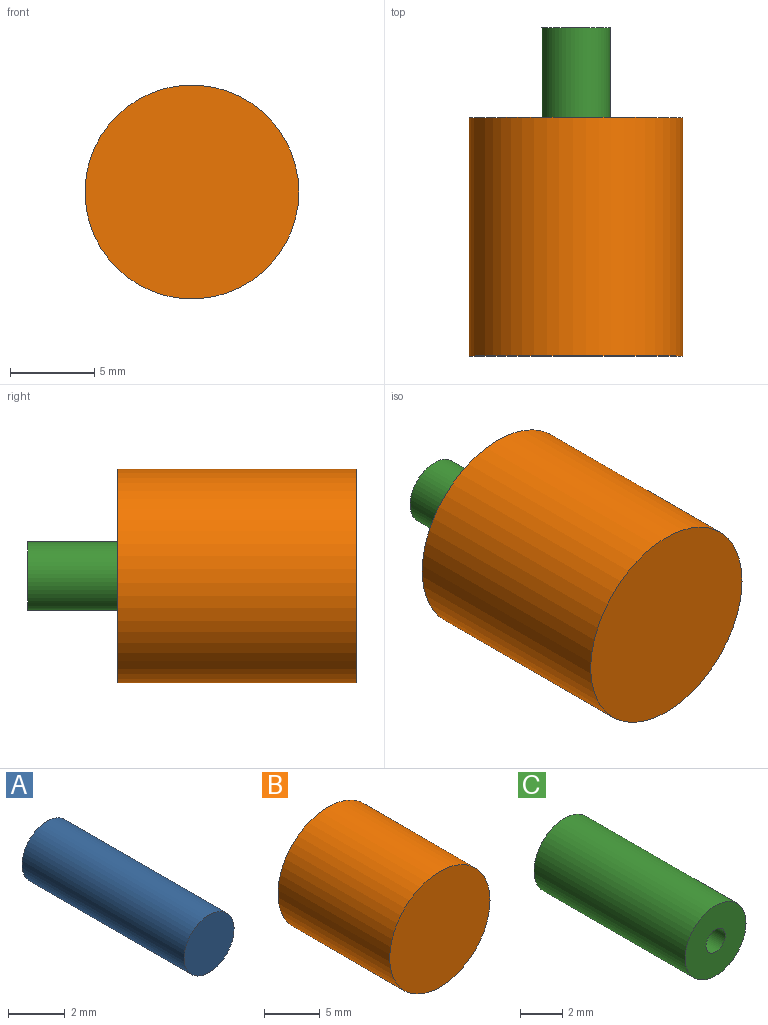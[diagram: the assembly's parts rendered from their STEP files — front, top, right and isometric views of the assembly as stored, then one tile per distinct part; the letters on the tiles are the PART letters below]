
ASSEMBLY  parts=3 mates=1
PART A: 3 faces, bbox 2.5x8.1x2.5 mm
  f0: cylinder r=1.24mm len=8.08mm, axis (0,1,0), area 63.2mm2, adj f1,f2
  f1: plane 2.49x2.49mm, normal (0,-1,0), area 4.9mm2, adj f0
  f2: plane 2.49x2.49mm, normal (0,1,0), area 4.9mm2, adj f0
PART B: 5 faces, bbox 12.7x14.2x12.7 mm
  f0: cylinder r=2.11mm len=4.83mm, axis (0,1,0), area 63.9mm2, adj f2,f3
  f1: cylinder r=6.35mm len=14.16mm, axis (0,1,0), area 565mm2, adj f2,f4
  f2: plane 12.7x12.7mm, normal (0,1,0), area 112.7mm2, adj f0,f1
  f3: plane 4.22x4.22mm, normal (0,1,0), area 14mm2, adj f0
  f4: plane 12.7x12.7mm, normal (0,-1,0), area 126.7mm2, adj f1
PART C: 4 faces, bbox 4.1x10.2x4.1 mm
  f0: cylinder r=2.04mm len=10.16mm, axis (0,1,0), area 130.5mm2, adj f1,f2
  f1: plane 4.09x4.09mm, normal (0,-1,0), area 11.8mm2, adj f0,f3
  f2: plane 4.09x4.09mm, normal (0,1,0), area 11.8mm2, adj f0,f3
  f3: cylinder r=0.65mm len=10.16mm, axis (0,1,0), area 41.3mm2, adj f1,f2
PLACE A t=(-8.13,1.87,-0.78)mm
PLACE B t=(-8.13,1.87,-0.78)mm
PLACE C t=(-8.13,7.2,-0.78)mm
MATE cylindrical C.f0 <-> B.f0  axis (0,1,0) through (-8.13,7.2,-0.78)mm
